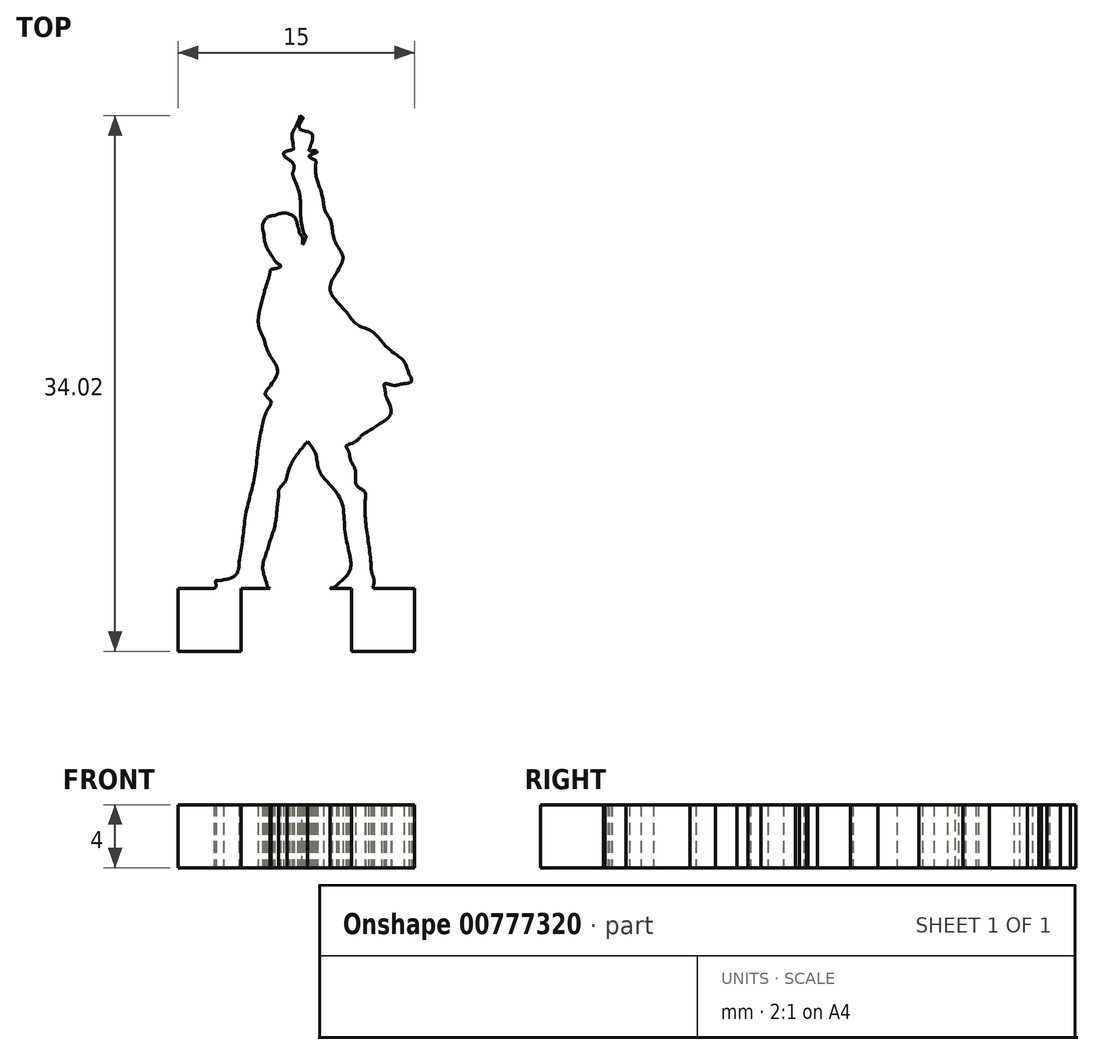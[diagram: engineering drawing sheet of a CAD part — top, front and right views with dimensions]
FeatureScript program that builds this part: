
annotation { "Feature Type Name" : "Feature", "Feature Type Description" : "" }
export const myFeature = defineFeature(function(context is Context, id is Id, definition is map)
    precondition{}
    {
        {
            var Q0;
            Q0=qCreatedBy(makeId("Top.planeOp"),FACE);
            var sketch = newSketch(context, id + "F0", { "sketchPlane" : qUnion([Q0])});
            skFitSpline(sketch, "E0", {"points": [v(-2.9, -14.64) * mm, v(-3.14, -13.66) * mm, v(-2.91, -12.76) * mm, v(-2.63, -11.83) * mm]});
            skFitSpline(sketch, "E1", {"points": [v(-2.63, -11.83) * mm, v(-2.36, -10.96) * mm, v(-2.24, -10.04) * mm, v(-2.13, -9.13) * mm]});
            skFitSpline(sketch, "E2", {"points": [v(-2.13, -9.13) * mm, v(-2.07, -8.64) * mm, v(-1.75, -8.28) * mm, v(-1.6, -7.84) * mm]});
            skFitSpline(sketch, "E3", {"points": [v(-1.6, -7.84) * mm, v(-1.32, -7.06) * mm, v(-0.86, -6.36) * mm, v(-0.3, -5.68) * mm]});
            skFitSpline(sketch, "E4", {"points": [v(-0.3, -5.68) * mm, v(0.23, -6.51) * mm, v(0.42, -7.46) * mm, v(0.97, -8.26) * mm]});
            skFitSpline(sketch, "E5", {"points": [v(0.97, -8.26) * mm, v(1.88, -9.56) * mm, v(2.06, -11.1) * mm, v(2.32, -12.62) * mm]});
            skFitSpline(sketch, "E6", {"points": [v(2.32, -12.62) * mm, v(2.46, -13.46) * mm, v(2.3, -14.07) * mm, v(1.67, -14.7) * mm]});
            skFitSpline(sketch, "E7", {"points": [v(1.67, -14.7) * mm, v(1.47, -14.9) * mm, v(1.3, -14.97) * mm, v(1.12, -15) * mm]});
            skFitSpline(sketch, "E8", {"points": [v(3.9, -15) * mm, v(3.88, -14.98) * mm, v(3.87, -14.94) * mm, v(3.88, -14.89) * mm]});
            skFitSpline(sketch, "E9", {"points": [v(3.88, -14.89) * mm, v(3.92, -14.44) * mm, v(3.79, -14.02) * mm, v(3.74, -13.58) * mm]});
            skFitSpline(sketch, "E10", {"points": [v(3.74, -13.58) * mm, v(3.6, -12.23) * mm, v(3.4, -10.87) * mm, v(3.35, -9.51) * mm]});
            skFitSpline(sketch, "E11", {"points": [v(3.35, -9.51) * mm, v(3.32, -8.87) * mm, v(2.83, -8.49) * mm, v(2.76, -7.9) * mm]});
            skFitSpline(sketch, "E12", {"points": [v(2.76, -7.9) * mm, v(2.71, -7.42) * mm, v(2.48, -6.98) * mm, v(2.36, -6.5) * mm]});
            skFitSpline(sketch, "E13", {"points": [v(2.36, -6.5) * mm, v(2.3, -6.28) * mm, v(2.16, -5.99) * mm, v(2.47, -5.82) * mm]});
            skFitSpline(sketch, "E14", {"points": [v(2.47, -5.82) * mm, v(2.88, -5.6) * mm, v(3.19, -5.26) * mm, v(3.58, -5.01) * mm]});
            skFitSpline(sketch, "E15", {"points": [v(3.58, -5.01) * mm, v(4.39, -4.5) * mm, v(5, -3.9) * mm, v(4.69, -2.82) * mm]});
            skFitSpline(sketch, "E16", {"points": [v(4.69, -2.82) * mm, v(4.66, -2.74) * mm, v(4.66, -2.65) * mm, v(4.65, -2.57) * mm]});
            skFitSpline(sketch, "E17", {"points": [v(4.65, -2.57) * mm, v(4.6, -2.27) * mm, v(4.58, -2.03) * mm, v(5.03, -2.09) * mm]});
            skFitSpline(sketch, "E18", {"points": [v(5.03, -2.09) * mm, v(5.29, -2.12) * mm, v(5.57, -2.06) * mm, v(5.84, -2) * mm]});
            skFitSpline(sketch, "E19", {"points": [v(5.84, -2) * mm, v(6.17, -1.95) * mm, v(6.32, -1.82) * mm, v(6.15, -1.42) * mm]});
            skFitSpline(sketch, "E20", {"points": [v(6.15, -1.42) * mm, v(5.77, -0.53) * mm, v(5.05, 0.04) * mm, v(4.4, 0.69) * mm]});
            skFitSpline(sketch, "E21", {"points": [v(4.4, 0.69) * mm, v(3.74, 1.34) * mm, v(2.88, 1.73) * mm, v(2.26, 2.43) * mm]});
            skFitSpline(sketch, "E22", {"points": [v(2.26, 2.43) * mm, v(1.59, 3.19) * mm, v(1.13, 4.02) * mm, v(1.53, 5.03) * mm]});
            skFitSpline(sketch, "E23", {"points": [v(1.53, 5.03) * mm, v(1.94, 6.04) * mm, v(1.5, 6.93) * mm, v(1.27, 7.84) * mm]});
            skFitSpline(sketch, "E24", {"points": [v(1.27, 7.84) * mm, v(1.14, 8.4) * mm, v(0.84, 8.94) * mm, v(0.71, 9.5) * mm]});
            skFitSpline(sketch, "E25", {"points": [v(0.71, 9.5) * mm, v(0.53, 10.3) * mm, v(0.26, 11.1) * mm, v(0.22, 11.92) * mm]});
            skFitSpline(sketch, "E26", {"points": [v(0.22, 11.92) * mm, v(0.21, 12.16) * mm, v(-0.19, 12.42) * mm, v(0.25, 12.66) * mm]});
            skFitSpline(sketch, "E27", {"points": [v(0.25, 12.66) * mm, v(0.32, 12.7) * mm, v(0.2, 12.8) * mm, v(0.12, 12.8) * mm]});
            skFitSpline(sketch, "E28", {"points": [v(0.12, 12.8) * mm, v(-0.18, 12.8) * mm, v(-0.15, 12.94) * mm, v(-0.09, 13.16) * mm]});
            skFitSpline(sketch, "E29", {"points": [v(-0.09, 13.16) * mm, v(0.03, 13.54) * mm, v(-0.02, 13.86) * mm, v(-0.45, 14.03) * mm]});
            skFitSpline(sketch, "E30", {"points": [v(-0.45, 14.03) * mm, v(-0.73, 14.14) * mm, v(-0.83, 14.35) * mm, v(-0.7, 14.65) * mm]});
            skFitSpline(sketch, "E31", {"points": [v(-0.7, 14.65) * mm, v(-0.65, 14.74) * mm, v(-0.58, 14.86) * mm, v(-0.78, 15) * mm]});
            skFitSpline(sketch, "E32", {"points": [v(-0.78, 15) * mm, v(-0.98, 14.43) * mm, v(-1.26, 13.9) * mm, v(-1.23, 13.32) * mm]});
            skFitSpline(sketch, "E33", {"points": [v(-1.23, 13.32) * mm, v(-1.21, 13.06) * mm, v(-1.18, 12.9) * mm, v(-1.43, 12.8) * mm]});
            skFitSpline(sketch, "E34", {"points": [v(-1.43, 12.8) * mm, v(-1.8, 12.66) * mm, v(-1.75, 12.43) * mm, v(-1.5, 12.24) * mm]});
            skFitSpline(sketch, "E35", {"points": [v(-1.5, 12.24) * mm, v(-1.24, 12.01) * mm, v(-1.15, 11.74) * mm, v(-1.23, 11.42) * mm]});
            skFitSpline(sketch, "E36", {"points": [v(-1.23, 11.42) * mm, v(-1.26, 11.3) * mm, v(-1.22, 11.2) * mm, v(-1.18, 11.08) * mm]});
            skFitSpline(sketch, "E37", {"points": [v(-1.18, 11.08) * mm, v(-0.79, 9.94) * mm, v(-0.74, 8.73) * mm, v(-0.55, 7.55) * mm]});
            skFitSpline(sketch, "E38", {"points": [v(-0.55, 7.55) * mm, v(-0.4, 7.36) * mm, v(-0.43, 7.17) * mm, v(-0.6, 6.83) * mm]});
            skFitSpline(sketch, "E39", {"points": [v(-0.6, 6.83) * mm, v(-0.62, 7.1) * mm, v(-0.63, 7.23) * mm, v(-0.64, 7.36) * mm]});
            skFitSpline(sketch, "E40", {"points": [v(-0.64, 7.36) * mm, v(-0.8, 7.54) * mm, v(-0.85, 7.78) * mm, v(-0.93, 8) * mm]});
            skFitSpline(sketch, "E41", {"points": [v(-0.93, 8) * mm, v(-1.1, 8.54) * mm, v(-1.73, 8.82) * mm, v(-2.4, 8.66) * mm]});
            skFitSpline(sketch, "E42", {"points": [v(-2.4, 8.66) * mm, v(-2.85, 8.56) * mm, v(-3.15, 8.09) * mm, v(-3.08, 7.55) * mm]});
            skFitSpline(sketch, "E43", {"points": [v(-3.08, 7.55) * mm, v(-3, 6.98) * mm, v(-2.79, 6.46) * mm, v(-2.48, 5.99) * mm]});
            skFitSpline(sketch, "E44", {"points": [v(-2.48, 5.99) * mm, v(-2.3, 5.71) * mm, v(-2, 5.45) * mm, v(-2.56, 5.26) * mm]});
            skFitSpline(sketch, "E45", {"points": [v(-2.56, 5.26) * mm, v(-2.63, 5.23) * mm, v(-2.67, 5.09) * mm, v(-2.7, 5) * mm]});
            skFitSpline(sketch, "E46", {"points": [v(-2.7, 5) * mm, v(-2.82, 4.54) * mm, v(-2.97, 4.09) * mm, v(-3.08, 3.63) * mm]});
            skFitSpline(sketch, "E47", {"points": [v(-3.08, 3.63) * mm, v(-3.33, 2.68) * mm, v(-3.42, 1.78) * mm, v(-3.07, 0.83) * mm]});
            skFitSpline(sketch, "E48", {"points": [v(-3.07, 0.83) * mm, v(-2.7, -0.16) * mm, v(-2.2, -1.17) * mm, v(-2.75, -2.26) * mm]});
            skFitSpline(sketch, "E49", {"points": [v(-2.75, -2.26) * mm, v(-2.97, -2.7) * mm, v(-2.6, -3.14) * mm, v(-2.8, -3.58) * mm]});
            skFitSpline(sketch, "E50", {"points": [v(-2.8, -3.58) * mm, v(-2.95, -3.89) * mm, v(-3.07, -4.21) * mm, v(-3.14, -4.54) * mm]});
            skFitSpline(sketch, "E51", {"points": [v(-3.14, -4.54) * mm, v(-3.43, -6.05) * mm, v(-3.6, -7.57) * mm, v(-3.93, -9.08) * mm]});
            skFitSpline(sketch, "E52", {"points": [v(-3.93, -9.08) * mm, v(-4.25, -10.48) * mm, v(-4.42, -11.92) * mm, v(-4.63, -13.35) * mm]});
            skFitSpline(sketch, "E53", {"points": [v(-4.63, -13.35) * mm, v(-4.72, -13.95) * mm, v(-5.04, -14.3) * mm, v(-5.61, -14.46) * mm]});
            skFitSpline(sketch, "E54", {"points": [v(-5.61, -14.46) * mm, v(-5.8, -14.5) * mm, v(-6.12, -14.52) * mm, v(-6.12, -14.73) * mm]});
            skFitSpline(sketch, "E55", {"points": [v(-6.12, -14.73) * mm, v(-6.12, -14.9) * mm, v(-6.16, -14.97) * mm, v(-6.22, -15) * mm]});
            skLineSegment(sketch, "E56", {"start": v(1.12, -15) * mm, "end": v(3.9, -15) * mm});
            skFitSpline(sketch, "E57", {"points": [v(-2.69, -15) * mm, v(-2.8, -14.96) * mm, v(-2.86, -14.85) * mm, v(-2.9, -14.64) * mm]});
            skLineSegment(sketch, "E58", {"start": v(-6.22, -15) * mm, "end": v(-2.69, -15) * mm});
            skLineSegment(sketch, "E59.bottom", {"start": v(-8.51, -15) * mm, "end": v(-4.51, -15) * mm});
            skLineSegment(sketch, "E59.top", {"start": v(-8.51, -19) * mm, "end": v(-4.51, -19) * mm});
            skLineSegment(sketch, "E59.left", {"start": v(-8.51, -15) * mm, "end": v(-8.51, -19) * mm});
            skLineSegment(sketch, "E59.right", {"start": v(-4.51, -15) * mm, "end": v(-4.51, -19) * mm});
            skLineSegment(sketch, "E60.bottom", {"start": v(2.49, -15) * mm, "end": v(6.49, -15) * mm});
            skLineSegment(sketch, "E60.top", {"start": v(2.49, -19) * mm, "end": v(6.49, -19) * mm});
            skLineSegment(sketch, "E60.left", {"start": v(2.49, -15) * mm, "end": v(2.49, -19) * mm});
            skLineSegment(sketch, "E60.right", {"start": v(6.49, -15) * mm, "end": v(6.49, -19) * mm});
            skSolve(sketch);
        }
        {
            var Q0;
            Q0=qSketchRegion(id+"F0",true);
            extrude(context, id + "F1", {"entities" : qUnion([Q0]), "endBound" : BoundingType.SYMMETRIC, "depth" : 4 * mm, "offsetDistance" : 25 * mm});
        }
    });
